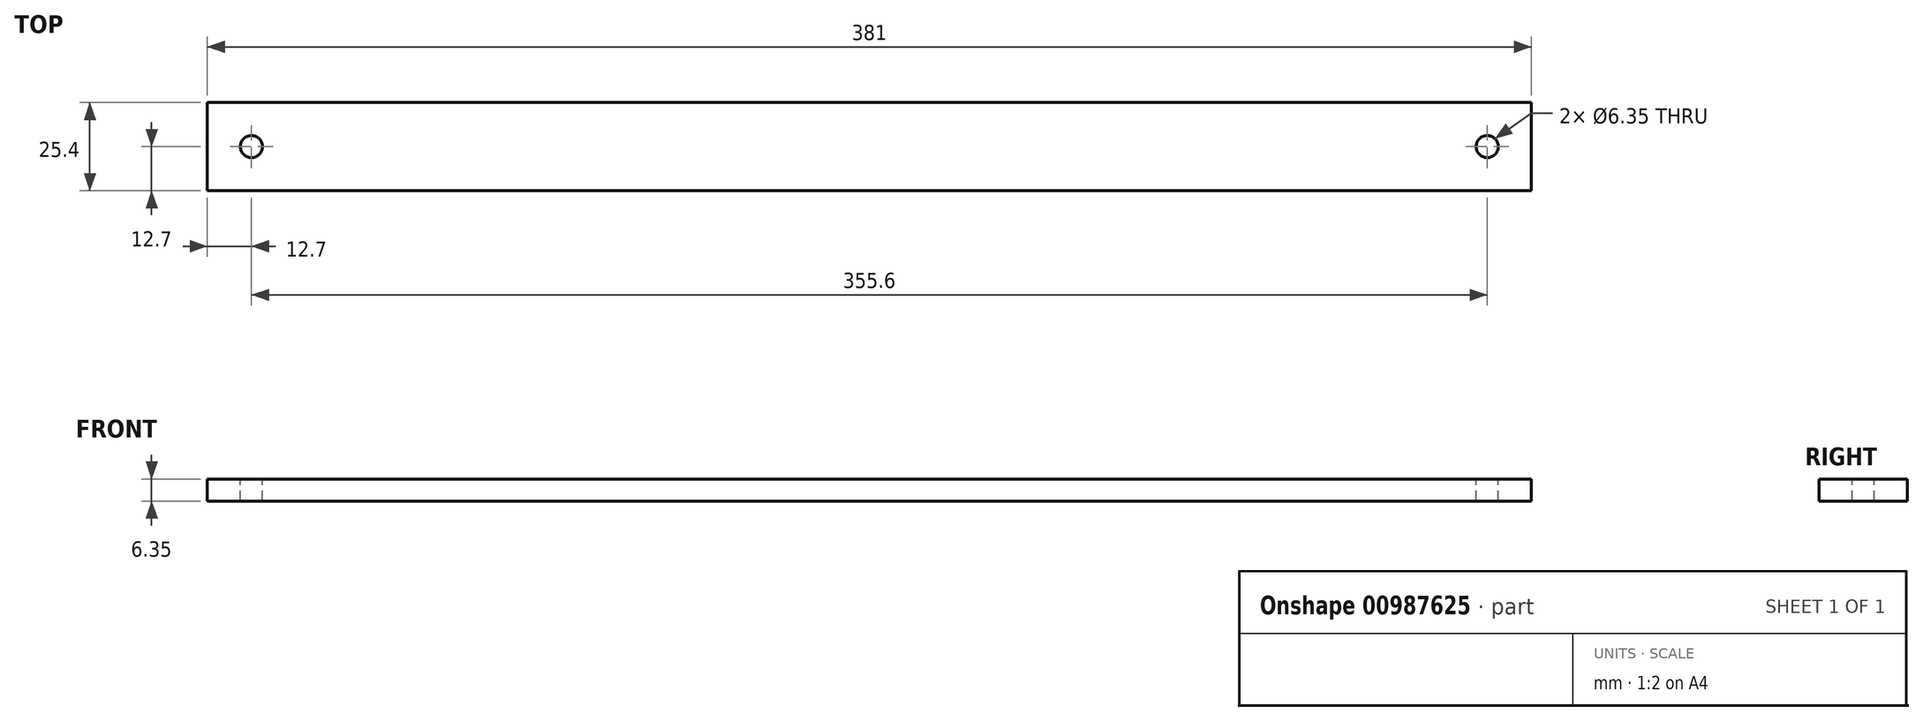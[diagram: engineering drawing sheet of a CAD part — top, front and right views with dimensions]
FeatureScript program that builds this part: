
annotation { "Feature Type Name" : "Feature", "Feature Type Description" : "" }
export const myFeature = defineFeature(function(context is Context, id is Id, definition is map)
    precondition{}
    {
        {
            var Q0;
            Q0=qCreatedBy(makeId("Top.planeOp"),FACE);
            var sketch = newSketch(context, id + "F0", { "sketchPlane" : qUnion([Q0])});
            skLineSegment(sketch, "E0.bottom", {"start": v(190.5, 12.7) * mm, "end": v(-190.5, 12.7) * mm});
            skLineSegment(sketch, "E0.top", {"start": v(190.5, -12.7) * mm, "end": v(-190.5, -12.7) * mm});
            skLineSegment(sketch, "E0.left", {"start": v(190.5, 12.7) * mm, "end": v(190.5, -12.7) * mm});
            skLineSegment(sketch, "E0.right", {"start": v(-190.5, 12.7) * mm, "end": v(-190.5, -12.7) * mm});
            skPoint(sketch, "E0.middle", {"position": v(0, 0) * mm});
            skSolve(sketch);
        }
        {
            var Q0;
            Q0=makeQuery(id+"F0.imprint","IMPRINT",FACE,{"disambiguationData":[TD([[makeQuery(id+"F0.imprint","IMPRINT",EDGE,{"derivedFrom":sQuery(id+"F0.wireOp",EDGE,"E0.bottom")}),1.0]])]});
            extrude(context, id + "F1", {"entities" : qUnion([Q0]), "depth" : 6.35 * mm, "offsetDistance" : 25.4 * mm});
        }
        {
            var Q0;
            Q0=makeQuery(id+"F1.opExtrude","CAP_FACE",FACE,{"disambiguationData":[OSD([sQuery(id+"F0.wireOp",EDGE,"E0.bottom"),sQuery(id+"F0.wireOp",EDGE,"E0.top"),sQuery(id+"F0.wireOp",EDGE,"E0.left"),sQuery(id+"F0.wireOp",EDGE,"E0.right")])],"isStart":false});
            var sketch = newSketch(context, id + "F2", { "sketchPlane" : qUnion([Q0])});
            skCircle(sketch, "E1", {"center": v(-177.8, 0) * mm, "radius": 3.18 * mm});
            skCircle(sketch, "E2", {"center": v(177.8, 0) * mm, "radius": 3.18 * mm});
            skSolve(sketch);
        }
        {
            var Q0;
            Q0=makeQuery(id+"F2.imprint","IMPRINT",FACE,{"disambiguationData":[TD([[makeQuery(id+"F2.imprint","IMPRINT",EDGE,{"derivedFrom":sQuery(id+"F2.wireOp",EDGE,"E1")}),1.0]])]});
            var Q1;
            Q1=makeQuery(id+"F2.imprint","IMPRINT",FACE,{"disambiguationData":[TD([[makeQuery(id+"F2.imprint","IMPRINT",EDGE,{"derivedFrom":sQuery(id+"F2.wireOp",EDGE,"HSciwoJY-czGO-I8cK-QoOT-NIAWDVXsKSCW")}),1.0]])]});
            var Q2;
            Q2=makeQuery(id+"F2.imprint","IMPRINT",FACE,{"disambiguationData":[TD([[makeQuery(id+"F2.imprint","IMPRINT",EDGE,{"derivedFrom":sQuery(id+"F2.wireOp",EDGE,"X6BEz2VU-xO08-x1DG-znvQ-mQdWGnIUGwx5")}),1.0]])]});
            var Q3;
            Q3=makeQuery(id+"F2.imprint","IMPRINT",FACE,{"disambiguationData":[TD([[makeQuery(id+"F2.imprint","IMPRINT",EDGE,{"derivedFrom":sQuery(id+"F2.wireOp",EDGE,"cy1oXDK6-yAg2-nr7p-gQgM-YkVIc5oMSGIw")}),1.0]])]});
            var Q4;
            Q4=makeQuery(id+"F2.imprint","IMPRINT",FACE,{"disambiguationData":[TD([[makeQuery(id+"F2.imprint","IMPRINT",EDGE,{"derivedFrom":sQuery(id+"F2.wireOp",EDGE,"TGx5rOfE-izY3-KCsG-E8Go-SMexTzZnK0EW")}),1.0]])]});
            var Q5;
            Q5=makeQuery(id+"F2.imprint","IMPRINT",FACE,{"disambiguationData":[TD([[makeQuery(id+"F2.imprint","IMPRINT",EDGE,{"derivedFrom":sQuery(id+"F2.wireOp",EDGE,"E2")}),1.0]])]});
            extrude(context, id + "F3", {"entities" : qUnion([Q0, Q1, Q2, Q3, Q4, Q5]), "operationType" : NewBodyOperationType.REMOVE, "oppositeDirection" : true, "depth" : 25.4 * mm, "offsetDistance" : 25.4 * mm});
        }
    });
